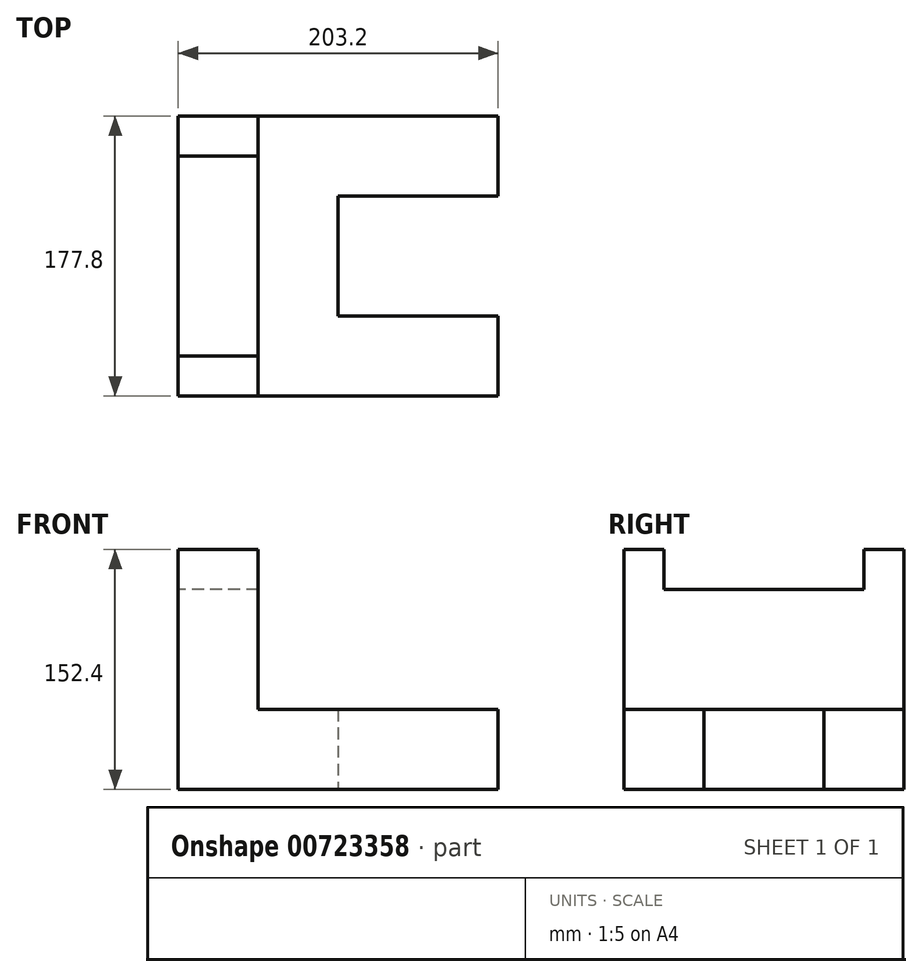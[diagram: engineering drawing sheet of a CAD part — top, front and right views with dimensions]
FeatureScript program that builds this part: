
annotation { "Feature Type Name" : "Feature", "Feature Type Description" : "" }
export const myFeature = defineFeature(function(context is Context, id is Id, definition is map)
    precondition{}
    {
        {
            var Q0;
            Q0=qCreatedBy(makeId("Front.planeOp"),FACE);
            var sketch = newSketch(context, id + "F0", { "sketchPlane" : qUnion([Q0])});
            skLineSegment(sketch, "E0", {"start": v(-99.25, -26.43) * mm, "end": v(103.95, -26.43) * mm});
            skLineSegment(sketch, "E1", {"start": v(103.95, -26.43) * mm, "end": v(103.95, 24.37) * mm});
            skLineSegment(sketch, "E2", {"start": v(103.95, 24.37) * mm, "end": v(-48.45, 24.37) * mm});
            skLineSegment(sketch, "E3", {"start": v(-48.45, 24.37) * mm, "end": v(-48.45, 100.57) * mm});
            skLineSegment(sketch, "E4", {"start": v(-48.45, 100.57) * mm, "end": v(-99.25, 100.57) * mm});
            skLineSegment(sketch, "E5", {"start": v(-99.25, 100.57) * mm, "end": v(-99.25, -26.43) * mm});
            skSolve(sketch);
        }
        {
            var Q0;
            Q0=makeQuery(id+"F0.imprint","IMPRINT",FACE,{"disambiguationData":[TD([[makeQuery(id+"F0.imprint","IMPRINT",EDGE,{"derivedFrom":sQuery(id+"F0.wireOp",EDGE,"E0")}),1.0]])]});
            extrude(context, id + "F1", {"entities" : qUnion([Q0]), "depth" : 177.8 * mm, "offsetDistance" : 25.4 * mm});
        }
        {
            var Q0;
            Q0=makeQuery(id+"F1.opExtrude","SWEPT_FACE",FACE,{"disambiguationData":[OSD([sQuery(id+"F0.wireOp",EDGE,"E4")])]});
            var sketch = newSketch(context, id + "F2", { "sketchPlane" : qUnion([Q0])});
            skLineSegment(sketch, "E6", {"start": v(-99.25, -177.8) * mm, "end": v(-99.25, -152.4) * mm});
            skLineSegment(sketch, "E7", {"start": v(-99.25, -152.4) * mm, "end": v(-48.45, -152.4) * mm});
            skLineSegment(sketch, "E8", {"start": v(-48.45, -152.4) * mm, "end": v(-48.45, -177.8) * mm});
            skLineSegment(sketch, "E9", {"start": v(-48.45, -177.8) * mm, "end": v(-99.25, -177.8) * mm});
            skSolve(sketch);
        }
        {
            var Q0;
            Q0=makeQuery(id+"F2.imprint","IMPRINT",FACE,{"disambiguationData":[TD([[makeQuery(id+"F2.imprint","IMPRINT",EDGE,{"derivedFrom":sQuery(id+"F2.wireOp",EDGE,"E6")}),-1.0]])]});
            extrude(context, id + "F3", {"entities" : qUnion([Q0]), "operationType" : NewBodyOperationType.ADD, "depth" : 25.4 * mm, "offsetDistance" : 25.4 * mm});
        }
        {
            var Q0;
            Q0=makeQuery(id+"F1.opExtrude","SWEPT_FACE",FACE,{"disambiguationData":[OSD([sQuery(id+"F0.wireOp",EDGE,"E4")])]});
            var sketch = newSketch(context, id + "F4", { "sketchPlane" : qUnion([Q0])});
            skLineSegment(sketch, "E10", {"start": v(-99.25, 0) * mm, "end": v(-48.45, 0) * mm});
            skLineSegment(sketch, "E11", {"start": v(-48.45, 0) * mm, "end": v(-48.45, -25.4) * mm});
            skLineSegment(sketch, "E12", {"start": v(-48.45, -25.4) * mm, "end": v(-99.25, -25.4) * mm});
            skLineSegment(sketch, "E13", {"start": v(-99.25, -25.4) * mm, "end": v(-99.25, 0) * mm});
            skSolve(sketch);
        }
        {
            var Q0;
            Q0=makeQuery(id+"F4.imprint","IMPRINT",FACE,{"disambiguationData":[TD([[makeQuery(id+"F4.imprint","IMPRINT",EDGE,{"derivedFrom":sQuery(id+"F4.wireOp",EDGE,"E10")}),1.0]])]});
            extrude(context, id + "F5", {"entities" : qUnion([Q0]), "operationType" : NewBodyOperationType.ADD, "depth" : 25.4 * mm, "offsetDistance" : 25.4 * mm});
        }
        {
            var Q0;
            Q0=makeQuery(id+"F1.opExtrude","SWEPT_FACE",FACE,{"disambiguationData":[OSD([sQuery(id+"F0.wireOp",EDGE,"E1")])]});
            var sketch = newSketch(context, id + "F6", { "sketchPlane" : qUnion([Q0])});
            skLineSegment(sketch, "E14", {"start": v(-177.8, -1.03) * mm, "end": v(-127, -1.03) * mm});
            skLineSegment(sketch, "E15", {"start": v(0, 0) * mm, "end": v(-50.8, 0) * mm});
            skLineSegment(sketch, "E16", {"start": v(-127, 24.37) * mm, "end": v(-127, -26.43) * mm});
            skLineSegment(sketch, "E17", {"start": v(-127, -26.43) * mm, "end": v(-50.8, -26.43) * mm});
            skLineSegment(sketch, "E18", {"start": v(-50.8, -26.43) * mm, "end": v(-50.8, 24.37) * mm});
            skLineSegment(sketch, "E19", {"start": v(-50.8, 24.37) * mm, "end": v(-127, 24.37) * mm});
            skSolve(sketch);
        }
        {
            var Q0;
            {var subQ2=sQuery(id+"F6.wireOp",EDGE,"E17");Q0=makeQuery(id+"F6.imprint","IMPRINT",FACE,{"disambiguationData":[TD([[makeQuery(id+"F6.imprint","IMPRINT",EDGE,{"derivedFrom":subQ2}),1.0]])]});}
            extrude(context, id + "F7", {"entities" : qUnion([Q0]), "operationType" : NewBodyOperationType.REMOVE, "oppositeDirection" : true, "depth" : 101.6 * mm, "offsetDistance" : 25.4 * mm});
        }
    });
